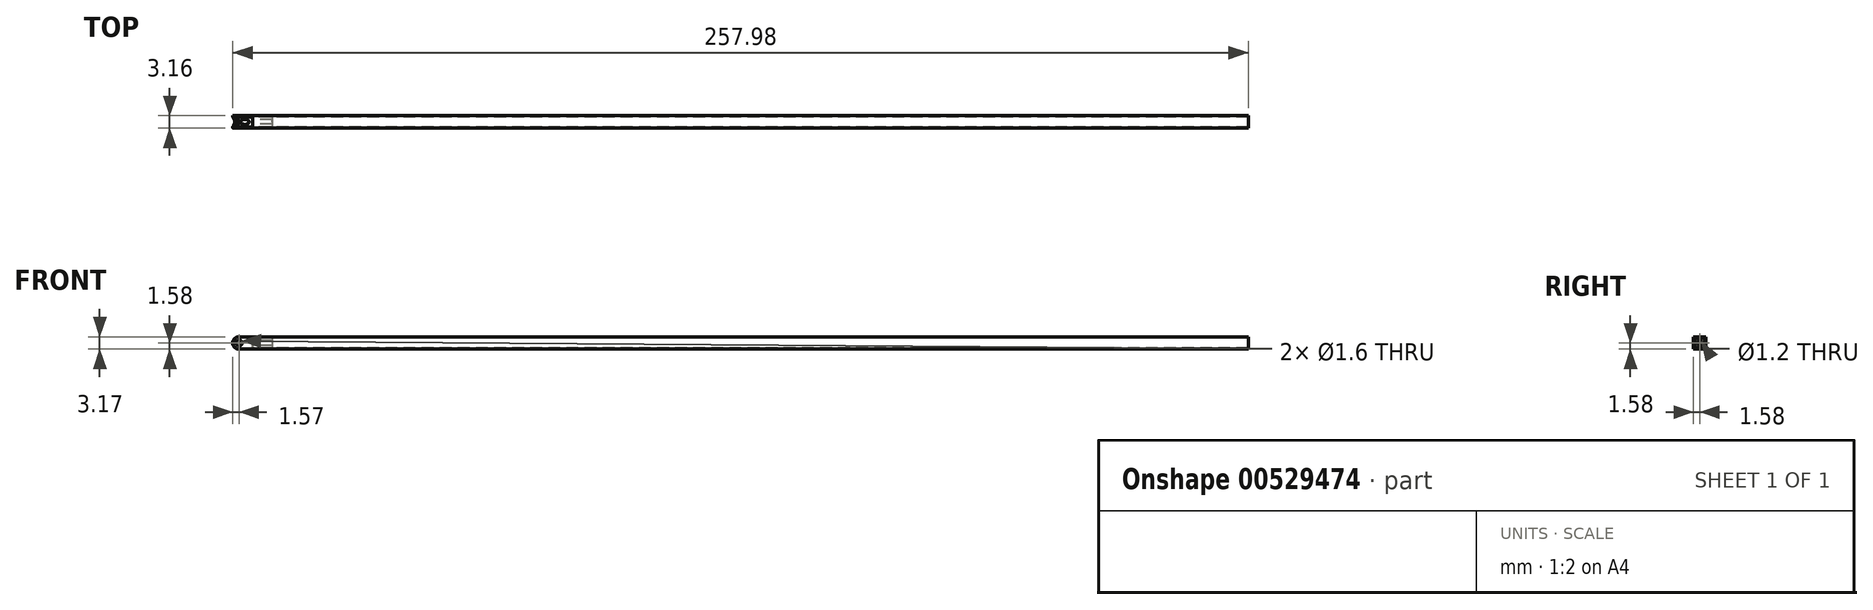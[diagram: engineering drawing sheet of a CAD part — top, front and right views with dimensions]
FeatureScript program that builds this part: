
annotation { "Feature Type Name" : "Feature", "Feature Type Description" : "" }
export const myFeature = defineFeature(function(context is Context, id is Id, definition is map)
    precondition{}
    {
        {
            var Q0;
            Q0=qCreatedBy(makeId("Front.planeOp"),FACE);
            var sketch = newSketch(context, id + "F0", { "sketchPlane" : qUnion([Q0])});
            skCircle(sketch, "E0", {"center": v(0, 0) * mm, "radius": 1.6 * mm});
            skLineSegment(sketch, "E1.bottom", {"start": v(0, 1.6) * mm, "end": v(3.41, 1.6) * mm});
            skLineSegment(sketch, "E1.top", {"start": v(0, -1.59) * mm, "end": v(3.4, -1.59) * mm});
            skLineSegment(sketch, "E1.left", {"start": v(0, 1.6) * mm, "end": v(0, -1.59) * mm});
            skLineSegment(sketch, "E1.right", {"start": v(3.41, 1.59) * mm, "end": v(3.4, -1.59) * mm});
            skSolve(sketch);
        }
        {
            var Q0;
            Q0 = qSketchRegion(id + "F0", true);
            extrude(context, id + "F1", {"entities" : qUnion([Q0]), "endBound" : BoundingType.SYMMETRIC, "depth" : 2.5 * mm, "offsetDistance" : 25 * mm});
        }
        {
            var Q0;
            Q0=makeQuery(id+"F1.opExtrude","SWEPT_FACE",FACE,{"disambiguationData":[OSD([sQuery(id+"F0.wireOp",EDGE,"E1.right")])]});
            var sketch = newSketch(context, id + "F2", { "sketchPlane" : qUnion([Q0])});
            skLineSegment(sketch, "E2.bottom", {"start": v(1.25, -1.25) * mm, "end": v(-1.25, -1.25) * mm});
            skLineSegment(sketch, "E2.top", {"start": v(1.25, 1.25) * mm, "end": v(-1.25, 1.25) * mm});
            skLineSegment(sketch, "E2.left", {"start": v(1.25, -1.25) * mm, "end": v(1.25, 1.25) * mm});
            skLineSegment(sketch, "E2.right", {"start": v(-1.25, -1.25) * mm, "end": v(-1.25, 1.25) * mm});
            skPoint(sketch, "E2.middle", {"position": v(0, 0) * mm});
            skSolve(sketch);
        }
        {
            var Q0;
            Q0 = qSketchRegion(id + "F2", true);
            extrude(context, id + "F3", {"entities" : qUnion([Q0]), "operationType" : NewBodyOperationType.ADD, "depth" : 5 * mm, "offsetDistance" : 25 * mm});
        }
        {
            var Q0;
            Q0=qCreatedBy(makeId("Right.planeOp"),FACE);
            cPlane(context, id + "F4", {"entities" : qUnion([Q0]), "cplaneType" : CPlaneType.OFFSET, "offset" : 2 * mm, "oppositeDirection" : true, "width" : 150 * mm, "height" : 150 * mm});
        }
        {
            var Q0;
            Q0=qCreatedBy(id+"F4.planeOp",FACE);
            var sketch = newSketch(context, id + "F5", { "sketchPlane" : qUnion([Q0])});
            skCircle(sketch, "E3", {"center": v(0, 0) * mm, "radius": 1.5 * mm});
            skSolve(sketch);
        }
        {
            var Q0;
            Q0 = qSketchRegion(id + "F5", true);
            extrude(context, id + "F6", {"entities" : qUnion([Q0]), "operationType" : NewBodyOperationType.REMOVE, "depth" : 6 * mm, "offsetDistance" : 25 * mm, "hasDraft" : true, "draftAngle" : 35 * degree, "draftPullDirection" : true});
        }
        {
            var Q0;
            Q0=qCreatedBy(id+"F4.planeOp",FACE);
            var sketch = newSketch(context, id + "F7", { "sketchPlane" : qUnion([Q0])});
            skCircle(sketch, "E4", {"center": v(0, 0) * mm, "radius": 0.6 * mm});
            skSolve(sketch);
        }
        {
            var Q0;
            Q0 = qSketchRegion(id + "F7", true);
            extrude(context, id + "F8", {"entities" : qUnion([Q0]), "operationType" : NewBodyOperationType.REMOVE, "depth" : 25 * mm, "offsetDistance" : 25 * mm});
        }
        {
            var Q0;
            Q0=makeQuery(id+"F8.boolean.opBoolean","INTERSECT",EDGE,{"derivedFrom":[makeQuery(id+"F6.boolean.opBoolean","COPY",FACE,{"derivedFrom":makeQuery(id+"F6.opExtrude","SWEPT_FACE",FACE,{"disambiguationData":[OSD([sQuery(id+"F5.wireOp",EDGE,"E3")])]})}),makeQuery(id+"F8.opExtrude","SWEPT_FACE",FACE,{"disambiguationData":[OSD([sQuery(id+"F7.wireOp",EDGE,"E4")])]})]});
            fillet(context, id + "F9", {"entities" : qUnion([Q0]), "radius" : 1 * mm, "tangentPropagation" : true, "allowEdgeOverflow" : false});
        }
        {
            var Q0;
            Q0=makeQuery(id+"F6.boolean.opBoolean","INTERSECT",EDGE,{"derivedFrom":[makeQuery(id+"F1.opExtrude","SWEPT_FACE",FACE,{"disambiguationData":[OSD([sQuery(id+"F0.wireOp",EDGE,"E0")])]}),makeQuery(id+"F6.opExtrude","SWEPT_FACE",FACE,{"disambiguationData":[OSD([sQuery(id+"F5.wireOp",EDGE,"E3")])]})]});
            fillet(context, id + "F10", {"entities" : qUnion([Q0]), "radius" : .3 * mm, "tangentPropagation" : true, "allowEdgeOverflow" : false});
        }
        {
            var Q0;
            Q0=makeQuery(id+"F3.boolean.opBoolean","MERGE",FACE,{"derivedFrom":[makeQuery(id+"F1.opExtrude","CAP_FACE",FACE,{"disambiguationData":[OSD([sQuery(id+"F0.wireOp",EDGE,"E0"),sQuery(id+"F0.wireOp",EDGE,"E1.bottom"),sQuery(id+"F0.wireOp",EDGE,"E1.top"),sQuery(id+"F0.wireOp",EDGE,"E1.right")])],"isStart":false}),makeQuery(id+"F3.opExtrude","SWEPT_FACE",FACE,{"disambiguationData":[OSD([sQuery(id+"F2.wireOp",EDGE,"E2.right")])]})]});
            var sketch = newSketch(context, id + "F11", { "sketchPlane" : qUnion([Q0])});
            skCircle(sketch, "E5", {"center": v(0, 0) * mm, "radius": 0.8 * mm});
            skSolve(sketch);
        }
        {
            var Q0;
            Q0 = qSketchRegion(id + "F11", true);
            extrude(context, id + "F12", {"entities" : qUnion([Q0]), "operationType" : NewBodyOperationType.REMOVE, "oppositeDirection" : true, "depth" : .5 * mm, "offsetDistance" : 25 * mm});
        }
        {
            var Q0;
            Q0=makeQuery(id+"F3.boolean.opBoolean","MERGE",FACE,{"derivedFrom":[makeQuery(id+"F1.opExtrude","CAP_FACE",FACE,{"disambiguationData":[OSD([sQuery(id+"F0.wireOp",EDGE,"E0"),sQuery(id+"F0.wireOp",EDGE,"E1.bottom"),sQuery(id+"F0.wireOp",EDGE,"E1.top"),sQuery(id+"F0.wireOp",EDGE,"E1.right")])],"isStart":true}),makeQuery(id+"F3.opExtrude","SWEPT_FACE",FACE,{"disambiguationData":[OSD([sQuery(id+"F2.wireOp",EDGE,"E2.left")])]})]});
            var sketch = newSketch(context, id + "F13", { "sketchPlane" : qUnion([Q0])});
            skCircle(sketch, "E6", {"center": v(0, 0) * mm, "radius": 0.8 * mm});
            skSolve(sketch);
        }
        {
            var Q0;
            Q0 = qSketchRegion(id + "F13", true);
            extrude(context, id + "F14", {"entities" : qUnion([Q0]), "operationType" : NewBodyOperationType.REMOVE, "oppositeDirection" : true, "depth" : .5 * mm, "offsetDistance" : 25 * mm});
        }
        {
            var Q0;
            Q0=makeQuery(id+"F1.opExtrude","SWEPT_EDGE",EDGE,{"disambiguationData":[OSD([sQuery(id+"F0.wireOp",EDGE,"E0"),sQuery(id+"F0.wireOp",EDGE,"E1.bottom"),sQuery(id+"F0.wireOp",EDGE,"E1.left")])]});
            cPlane(context, id + "F15", {"entities" : qUnion([Q0]), "cplaneType" : CPlaneType.LINE_ANGLE, "offset" : 25 * mm, "angle" : 50 * degree, "oppositeDirection" : true, "width" : 150 * mm, "height" : 150 * mm});
        }
        {
            var Q0;
            Q0=qCreatedBy(id+"F15.planeOp",FACE);
            var sketch = newSketch(context, id + "F16", { "sketchPlane" : qUnion([Q0])});
            skCircle(sketch, "E7", {"center": v(0, 2) * mm, "radius": 0.5 * mm});
            skSolve(sketch);
        }
        {
            var Q0;
            Q0 = qSketchRegion(id + "F16", true);
            extrude(context, id + "F17", {"entities" : qUnion([Q0]), "operationType" : NewBodyOperationType.REMOVE, "oppositeDirection" : true, "depth" : 3.68 * mm, "offsetDistance" : 25 * mm});
        }
        {
            var Q0;
            Q0=makeQuery(id+"F1.opExtrude","SWEPT_EDGE",EDGE,{"disambiguationData":[OSD([sQuery(id+"F0.wireOp",EDGE,"E0"),sQuery(id+"F0.wireOp",EDGE,"E1.top"),sQuery(id+"F0.wireOp",EDGE,"E1.left")])]});
            cPlane(context, id + "F18", {"entities" : qUnion([Q0]), "cplaneType" : CPlaneType.LINE_ANGLE, "offset" : 25 * mm, "angle" : 50 * degree, "width" : 150 * mm, "height" : 150 * mm});
        }
        {
            var Q0;
            Q0=qCreatedBy(id+"F18.planeOp",FACE);
            var sketch = newSketch(context, id + "F19", { "sketchPlane" : qUnion([Q0])});
            skCircle(sketch, "E8", {"center": v(0, -1.97) * mm, "radius": 0.5 * mm});
            skSolve(sketch);
        }
        {
            var Q0;
            Q0=makeQuery(id+"F19.imprint","IMPRINT",FACE,{"disambiguationData":[TD([[makeQuery(id+"F19.imprint","IMPRINT",EDGE,{"derivedFrom":sQuery(id+"F19.wireOp",EDGE,"E8")}),1.0]])]});
            extrude(context, id + "F20", {"entities" : qUnion([Q0]), "operationType" : NewBodyOperationType.REMOVE, "depth" : 3.5 * mm, "offsetDistance" : 25 * mm});
        }
        {
            var Q0;
            Q0=makeQuery(id+"F20.boolean.opBoolean","INTERSECT",EDGE,{"derivedFrom":[makeQuery(id+"F1.opExtrude","SWEPT_FACE",FACE,{"disambiguationData":[OSD([sQuery(id+"F0.wireOp",EDGE,"E1.top")])]}),makeQuery(id+"F20.opExtrude","SWEPT_FACE",FACE,{"disambiguationData":[OSD([sQuery(id+"F19.wireOp",EDGE,"E8")])]})]});
            var Q1;
            Q1=makeQuery(id+"F20.boolean.opBoolean","INTERSECT",EDGE,{"derivedFrom":[makeQuery(id+"F8.boolean.opBoolean","COPY",FACE,{"derivedFrom":makeQuery(id+"F8.opExtrude","SWEPT_FACE",FACE,{"disambiguationData":[OSD([sQuery(id+"F7.wireOp",EDGE,"E4")])]})}),makeQuery(id+"F20.opExtrude","SWEPT_FACE",FACE,{"disambiguationData":[OSD([sQuery(id+"F19.wireOp",EDGE,"E8")])]})]});
            var Q2;
            Q2=makeQuery(id+"F17.boolean.opBoolean","INTERSECT",EDGE,{"derivedFrom":[makeQuery(id+"F8.boolean.opBoolean","COPY",FACE,{"derivedFrom":makeQuery(id+"F8.opExtrude","SWEPT_FACE",FACE,{"disambiguationData":[OSD([sQuery(id+"F7.wireOp",EDGE,"E4")])]})}),makeQuery(id+"F17.opExtrude","SWEPT_FACE",FACE,{"disambiguationData":[OSD([sQuery(id+"F16.wireOp",EDGE,"E7")])]})]});
            var Q3;
            Q3=makeQuery(id+"F17.boolean.opBoolean","INTERSECT",EDGE,{"derivedFrom":[makeQuery(id+"F1.opExtrude","SWEPT_FACE",FACE,{"disambiguationData":[OSD([sQuery(id+"F0.wireOp",EDGE,"E1.bottom")])]}),makeQuery(id+"F17.opExtrude","SWEPT_FACE",FACE,{"disambiguationData":[OSD([sQuery(id+"F16.wireOp",EDGE,"E7")])]})]});
            fillet(context, id + "F21", {"entities" : qUnion([Q0, Q1, Q2, Q3]), "radius" : .2 * mm, "tangentPropagation" : true, "allowEdgeOverflow" : false});
        }
        {
            var Q0;
            Q0=makeQuery(id+"F3.opExtrude","CAP_FACE",FACE,{"disambiguationData":[OSD([sQuery(id+"F2.wireOp",EDGE,"E2.bottom"),sQuery(id+"F2.wireOp",EDGE,"E2.top"),sQuery(id+"F2.wireOp",EDGE,"E2.left"),sQuery(id+"F2.wireOp",EDGE,"E2.right")])],"isStart":false});
            var sketch = newSketch(context, id + "F22", { "sketchPlane" : qUnion([Q0])});
            skPoint(sketch, "E9.middle", {"position": v(0, 0) * mm});
            skLineSegment(sketch, "E10.0", {"start": v(1.58, 1.58) * mm, "end": v(1.58, -1.58) * mm});
            skLineSegment(sketch, "E10.1", {"start": v(1.58, 1.58) * mm, "end": v(-1.58, 1.58) * mm});
            skLineSegment(sketch, "E10.2", {"start": v(-1.58, 1.58) * mm, "end": v(-1.58, -1.58) * mm});
            skLineSegment(sketch, "E10.3", {"start": v(1.58, -1.58) * mm, "end": v(-1.58, -1.58) * mm});
            skSolve(sketch);
        }
        {
            var Q0;
            Q0=makeQuery(id+"F22.imprint","IMPRINT",FACE,{"disambiguationData":[TD([[makeQuery(id+"F22.imprint","IMPRINT",EDGE,{"derivedFrom":sQuery(id+"F22.wireOp",EDGE,"E10.0")}),-1.0]])]});
            extrude(context, id + "F23", {"entities" : qUnion([Q0]), "depth" : 248 * mm, "offsetDistance" : 25 * mm, "hasSecondDirection" : true, "secondDirectionOppositeDirection" : true, "secondDirectionDepth" : 10 * mm});
        }
        {
            var Q0;
            Q0=makeQuery(id+"F23.opExtrude","SWEPT_FACE",FACE,{"disambiguationData":[OSD([sQuery(id+"F22.wireOp",EDGE,"E10.2")])]});
            var sketch = newSketch(context, id + "F24", { "sketchPlane" : qUnion([Q0])});
            skPoint(sketch, "E11", {"position": v(0, 1.58) * mm});
            skPoint(sketch, "E12", {"position": v(0, -1.58) * mm});
            skLineSegment(sketch, "E13", {"start": v(-1.59, 1.58) * mm, "end": v(0, 1.58) * mm, "construction": true});
            skLineSegment(sketch, "E14", {"start": v(0, -1.58) * mm, "end": v(-1.59, -1.58) * mm, "construction": true});
            skSolve(sketch);
        }
        {
            var Q0;
            {var subQ0=sQuery(id+"F22.wireOp",EDGE,"E10.2");Q0=makeQuery(id+"F24.imprint","IMPRINT",FACE,{"disambiguationData":[TD([[makeQuery(id+"F24.imprint","IMPRINT",EDGE,{"derivedFrom":makeQuery(id+"F23.opExtrude","CAP_EDGE",EDGE,{"disambiguationData":[OSD([subQ0])],"isStart":true})}),1.0]])]});}
            var sketch = newSketch(context, id + "F25", { "sketchPlane" : qUnion([Q0])});
            skLineSegment(sketch, "E15", {"start": v(0, 1.6) * mm, "end": v(-1.6, 1.6) * mm});
            skLineSegment(sketch, "E16", {"start": v(-1.6, 1.6) * mm, "end": v(-1.59, -1.59) * mm});
            skLineSegment(sketch, "E17", {"start": v(-1.59, -1.59) * mm, "end": v(0, -1.59) * mm});
            skLineSegment(sketch, "E18.0", {"start": v(-1.5, -0.52) * mm, "end": v(-1.5, -0.52) * mm});
            skArc(sketch, "E19.0", {"start": v(-1.5, -0.52) * mm, "mid": v(-0.92, -1.3) * mm, "end": v(0, -1.6) * mm});
            skFitSpline(sketch, "E20.0", {"points": [v(-1.5, 0.52) * mm, v(-1.56, 0.35) * mm, v(-1.57, 0) * mm, v(-1.56, -0.35) * mm, v(-1.5, -0.52) * mm, v(-1.5, 0.52) * mm]});
            skArc(sketch, "E21.0", {"start": v(0, 1.6) * mm, "mid": v(-0.92, 1.3) * mm, "end": v(-1.5, 0.52) * mm});
            skFitSpline(sketch, "E22.0", {"points": [v(-1.5, -0.52) * mm, v(-1.56, -0.35) * mm, v(-1.57, 0) * mm, v(-1.56, 0.35) * mm, v(-1.5, 0.52) * mm]});
            skSolve(sketch);
        }
        {
            var Q0;
            {var subQ0=sQuery(id+"F25.wireOp",EDGE,"E22.0");Q0=makeQuery(id+"F25.imprint","IMPRINT",FACE,{"disambiguationData":[TD([[makeQuery(id+"F25.imprint","IMPRINT",EDGE,{"derivedFrom":subQ0}),1.0]])]});}
            extrude(context, id + "F26", {"entities" : qUnion([Q0]), "operationType" : NewBodyOperationType.REMOVE, "oppositeDirection" : true, "depth" : 25 * mm, "offsetDistance" : 25 * mm});
        }
        {
            var Q0;
            Q0=makeQuery(id+"F23.opExtrude","SWEPT_FACE",FACE,{"disambiguationData":[OSD([sQuery(id+"F22.wireOp",EDGE,"E10.1")])]});
            var sketch = newSketch(context, id + "F27", { "sketchPlane" : qUnion([Q0])});
            skLineSegment(sketch, "E23.bottom", {"start": v(3.4, 1.25) * mm, "end": v(-0.98, 1.25) * mm});
            skLineSegment(sketch, "E23.top", {"start": v(3.41, -1.25) * mm, "end": v(-0.98, -1.25) * mm});
            skLineSegment(sketch, "E23.left", {"start": v(3.4, 1.25) * mm, "end": v(3.41, -1.25) * mm});
            skLineSegment(sketch, "E23.right", {"start": v(-0.98, 1.25) * mm, "end": v(-0.98, -1.25) * mm});
            skSolve(sketch);
        }
        {
            var Q0;
            Q0 = qSketchRegion(id + "F27", true);
            extrude(context, id + "F28", {"entities" : qUnion([Q0]), "operationType" : NewBodyOperationType.REMOVE, "endBound" : BoundingType.THROUGH_ALL, "oppositeDirection" : true, "depth" : 25 * mm, "offsetDistance" : 25 * mm});
        }
        {
            var Q0;
            {var subQ0=sQuery(id+"F22.wireOp",EDGE,"E10.2");Q0=makeQuery(id+"F24.imprint","IMPRINT",FACE,{"disambiguationData":[TD([[makeQuery(id+"F24.imprint","IMPRINT",EDGE,{"derivedFrom":makeQuery(id+"F23.opExtrude","CAP_EDGE",EDGE,{"disambiguationData":[OSD([subQ0])],"isStart":true})}),1.0]])]});}
            var sketch = newSketch(context, id + "F29", { "sketchPlane" : qUnion([Q0])});
            skCircle(sketch, "E24", {"center": v(0, 0) * mm, "radius": 0.8 * mm});
            skSolve(sketch);
        }
        {
            var Q0;
            Q0 = qSketchRegion(id + "F29", true);
            extrude(context, id + "F30", {"entities" : qUnion([Q0]), "operationType" : NewBodyOperationType.REMOVE, "endBound" : BoundingType.THROUGH_ALL, "oppositeDirection" : true, "depth" : mm, "offsetDistance" : 25 * mm});
        }
    });
